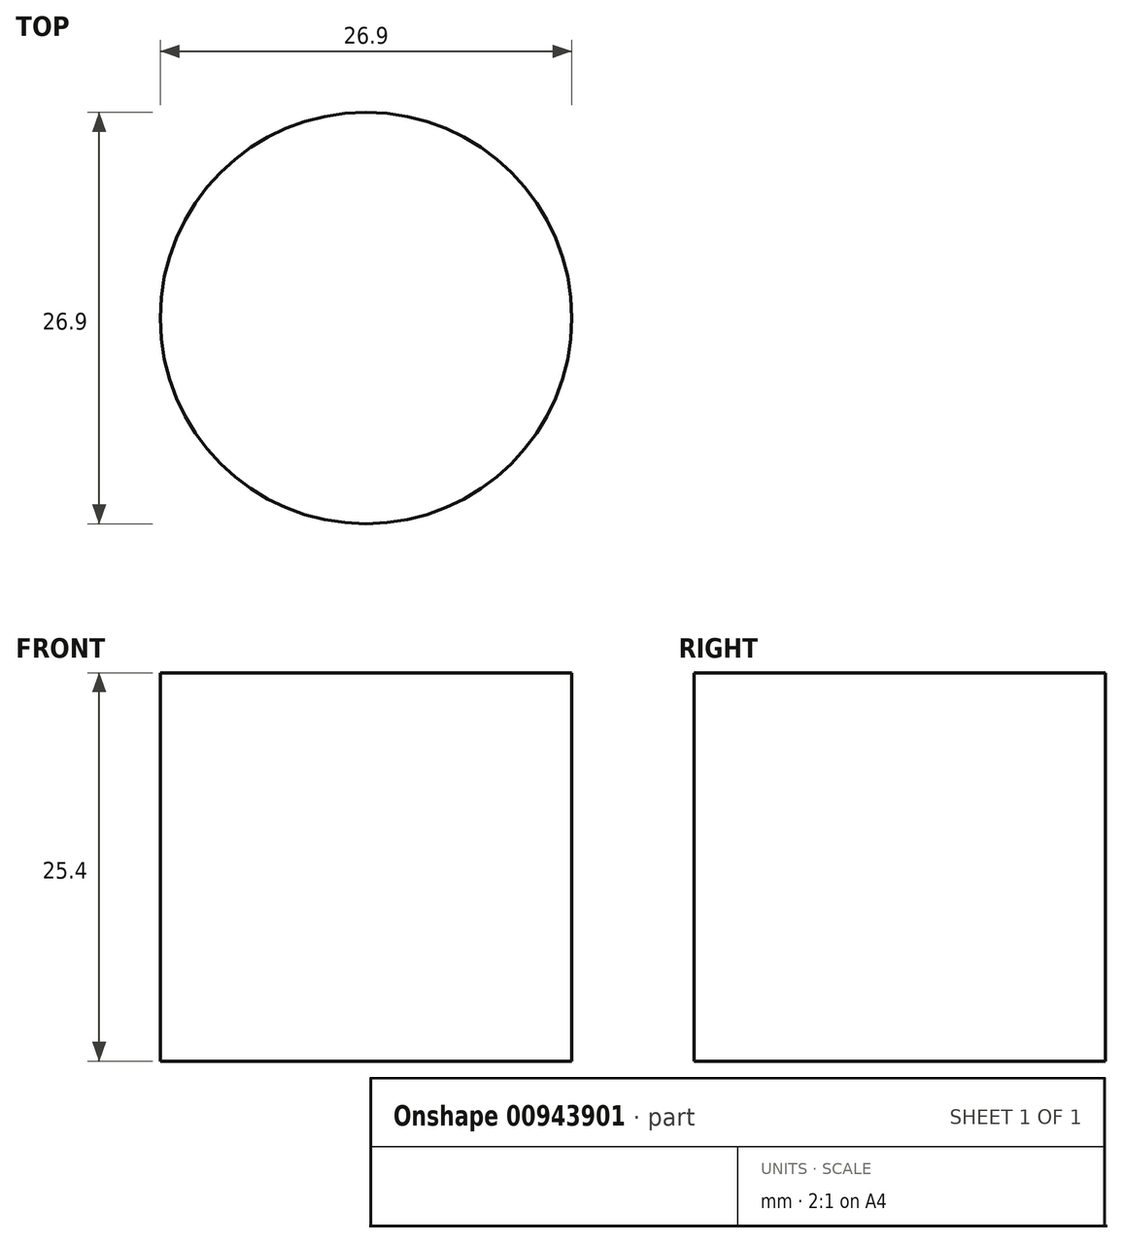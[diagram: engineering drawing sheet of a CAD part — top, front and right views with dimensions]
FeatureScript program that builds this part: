
annotation { "Feature Type Name" : "Feature", "Feature Type Description" : "" }
export const myFeature = defineFeature(function(context is Context, id is Id, definition is map)
    precondition{}
    {
        {
            var Q0;
            Q0=qCreatedBy(makeId("Top.planeOp"),FACE);
            var sketch = newSketch(context, id + "F0", { "sketchPlane" : qUnion([Q0])});
            skCircle(sketch, "E0", {"center": v(0, 0) * mm, "radius": 13.45 * mm});
            skSolve(sketch);
        }
        {
            var Q0;
            Q0 = qSketchRegion(id + "F0", true);
            extrude(context, id + "F1", {"entities" : qUnion([Q0]), "depth" : 25.4 * mm, "offsetDistance" : 25.4 * mm});
        }
    });
